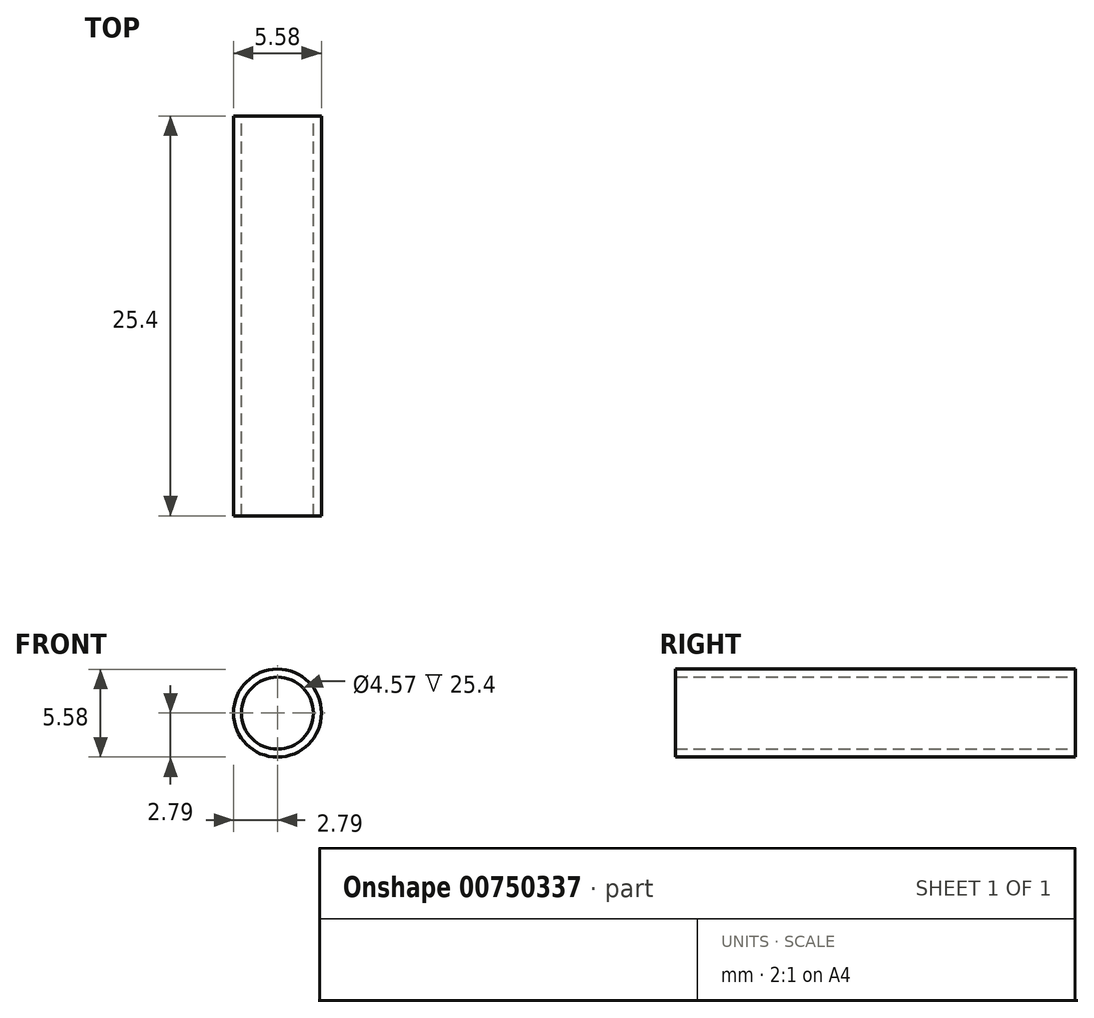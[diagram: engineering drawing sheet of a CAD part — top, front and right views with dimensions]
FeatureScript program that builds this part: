
annotation { "Feature Type Name" : "Feature", "Feature Type Description" : "" }
export const myFeature = defineFeature(function(context is Context, id is Id, definition is map)
    precondition{}
    {
        {
            var Q0;
            Q0=qCreatedBy(makeId("Front.planeOp"),FACE);
            var sketch = newSketch(context, id + "F0", { "sketchPlane" : qUnion([Q0])});
            skCircle(sketch, "E0", {"center": v(0, 0) * mm, "radius": 2.8 * mm});
            skCircle(sketch, "E1", {"center": v(0, 0) * mm, "radius": 2.29 * mm});
            skSolve(sketch);
        }
        {
            var Q0;
            Q0 = qSketchRegion(id + "F0", true);
            extrude(context, id + "F1", {"entities" : qUnion([Q0]), "depth" : 25.4 * mm, "offsetDistance" : 25.4 * mm});
        }
    });
